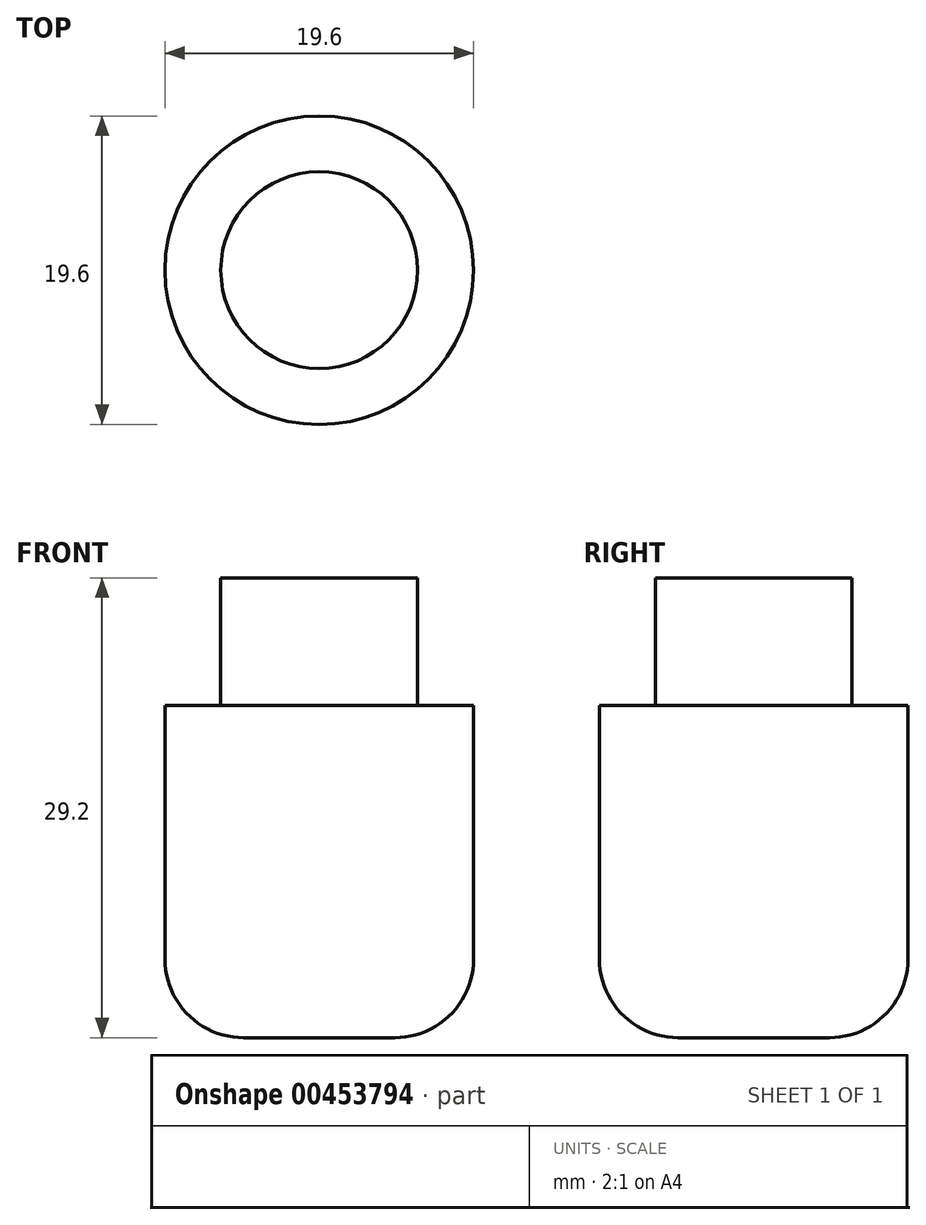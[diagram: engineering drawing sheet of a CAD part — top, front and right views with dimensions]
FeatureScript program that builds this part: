
annotation { "Feature Type Name" : "Feature", "Feature Type Description" : "" }
export const myFeature = defineFeature(function(context is Context, id is Id, definition is map)
    precondition{}
    {
        {
            var Q0;
            Q0=qCreatedBy(makeId("Top.planeOp"),FACE);
            var sketch = newSketch(context, id + "F0", { "sketchPlane" : qUnion([Q0])});
            skCircle(sketch, "E0", {"center": v(0, 0) * mm, "radius": 6.25 * mm});
            skSolve(sketch);
        }
        {
            var Q0;
            Q0 = qSketchRegion(id + "F0", true);
            extrude(context, id + "F1", {"entities" : qUnion([Q0]), "depth" : 8.1 * mm});
        }
        {
            var Q0;
            Q0=makeQuery(id+"F1.opExtrude","CAP_FACE",FACE,{"disambiguationData":[OSD([sQuery(id+"F0.wireOp",EDGE,"E0")])],"isStart":true});
            var sketch = newSketch(context, id + "F2", { "sketchPlane" : qUnion([Q0])});
            skCircle(sketch, "E1", {"center": v(0, 0) * mm, "radius": 9.8 * mm});
            skSolve(sketch);
        }
        {
            var Q0;
            Q0 = qSketchRegion(id + "F2", true);
            extrude(context, id + "F3", {"entities" : qUnion([Q0]), "operationType" : NewBodyOperationType.ADD, "depth" : 21.1 * mm});
        }
        {
            var Q0;
            Q0=makeQuery(id+"F3.opExtrude","CAP_EDGE",EDGE,{"disambiguationData":[OSD([sQuery(id+"F2.wireOp",EDGE,"E1")])],"isStart":false});
            fillet(context, id + "F4", {"entities" : qUnion([Q0]), "radius" : 5 * mm, "tangentPropagation" : true, "allowEdgeOverflow" : false});
        }
    });
